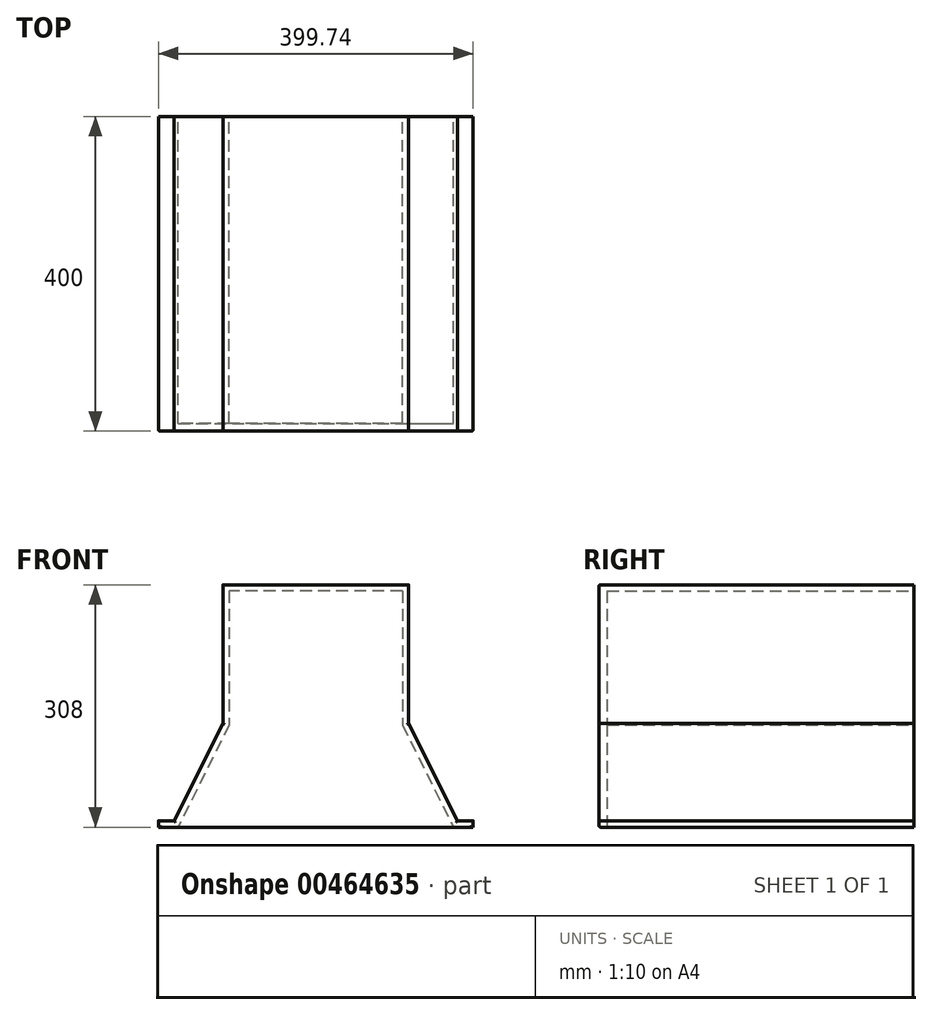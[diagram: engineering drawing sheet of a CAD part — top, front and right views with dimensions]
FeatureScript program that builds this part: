
annotation { "Feature Type Name" : "Feature", "Feature Type Description" : "" }
export const myFeature = defineFeature(function(context is Context, id is Id, definition is map)
    precondition{}
    {
        {
            var Q0;
            Q0=qCreatedBy(makeId("Front.planeOp"),FACE);
            var sketch = newSketch(context, id + "F0", { "sketchPlane" : qUnion([Q0])});
            skLineSegment(sketch, "E0", {"start": v(-131.02, -9.6) * mm, "end": v(-41.02, -9.6) * mm});
            skLineSegment(sketch, "E1.MirrorCS", {"start": v(-138.52, -1.6) * mm, "end": v(-138.52, 6.96) * mm});
            skLineSegment(sketch, "E2.MirrorCS", {"start": v(-131.02, 14.46) * mm, "end": v(-126.93, 14.46) * mm});
            skArc(sketch, "E3.MirrorCS", {"start": v(-131.02, -9.6) * mm, "mid": v(-136.51, -7.22) * mm, "end": v(-138.52, -1.6) * mm});
            skArc(sketch, "E4.MirrorCS", {"start": v(-138.52, 6.96) * mm, "mid": v(-136.33, 12.26) * mm, "end": v(-131.02, 14.46) * mm});
            skLineSegment(sketch, "E5.0", {"start": v(-131.02, 17.46) * mm, "end": v(-126.93, 17.46) * mm});
            skArc(sketch, "E5.1", {"start": v(-141.52, 6.96) * mm, "mid": v(-138.45, 14.38) * mm, "end": v(-131.02, 17.46) * mm});
            skLineSegment(sketch, "E5.2", {"start": v(-141.52, -1.5) * mm, "end": v(-141.52, 6.96) * mm});
            skArc(sketch, "E5.3", {"start": v(-141.53, -1.81) * mm, "mid": v(-141.53, -1.65) * mm, "end": v(-141.52, -1.5) * mm});
            skLineSegment(sketch, "E6", {"start": v(-93.76, -9.6) * mm, "end": v(-131.05, -9.6) * mm});
            skLineSegment(sketch, "E7.trimOffspring", {"start": v(-149.53, -9.6) * mm, "end": v(-199.87, -9.6) * mm});
            skLineSegment(sketch, "E8", {"start": v(-199.87, -9.6) * mm, "end": v(-199.87, -13.6) * mm});
            skLineSegment(sketch, "E9", {"start": v(-199.87, -13.6) * mm, "end": v(0.13, -13.6) * mm});
            skArc(sketch, "E10.filletArc", {"start": v(-149.53, -9.6) * mm, "mid": v(-143.95, -7.33) * mm, "end": v(-141.53, -1.81) * mm});
            skLineSegment(sketch, "E11", {"start": v(-49.36, -9.6) * mm, "end": v(0.13, -9.6) * mm});
            skArc(sketch, "E12.MirrorCS", {"start": v(141.8, -1.81) * mm, "mid": v(141.8, -1.65) * mm, "end": v(141.78, -1.5) * mm});
            skLineSegment(sketch, "E13.MirrorCS", {"start": v(138.78, -1.6) * mm, "end": v(138.78, 6.96) * mm});
            skLineSegment(sketch, "E14.MirrorCS", {"start": v(131.28, 14.46) * mm, "end": v(127.19, 14.46) * mm});
            skLineSegment(sketch, "E15.MirrorCS", {"start": v(200.13, -9.6) * mm, "end": v(200.13, -13.6) * mm});
            skLineSegment(sketch, "E16.MirrorCS", {"start": v(141.78, -1.5) * mm, "end": v(141.78, 6.96) * mm});
            skLineSegment(sketch, "E17.MirrorCS", {"start": v(131.28, 17.46) * mm, "end": v(127.19, 17.46) * mm});
            skArc(sketch, "E18.MirrorCS", {"start": v(131.28, -9.6) * mm, "mid": v(136.77, -7.22) * mm, "end": v(138.78, -1.6) * mm});
            skArc(sketch, "E19.MirrorCS", {"start": v(138.78, 6.96) * mm, "mid": v(136.59, 12.26) * mm, "end": v(131.28, 14.46) * mm});
            skLineSegment(sketch, "E20.MirrorCS", {"start": v(94.02, -9.6) * mm, "end": v(131.31, -9.6) * mm});
            skLineSegment(sketch, "E21.MirrorCS", {"start": v(131.28, -9.6) * mm, "end": v(41.28, -9.6) * mm});
            skLineSegment(sketch, "E22.MirrorCS", {"start": v(149.8, -9.6) * mm, "end": v(200.13, -9.6) * mm});
            skArc(sketch, "E23.MirrorCS", {"start": v(149.8, -9.6) * mm, "mid": v(144.21, -7.33) * mm, "end": v(141.8, -1.81) * mm});
            skArc(sketch, "E24.MirrorCS", {"start": v(141.78, 6.96) * mm, "mid": v(138.7, 14.38) * mm, "end": v(131.28, 17.46) * mm});
            skLineSegment(sketch, "E25", {"start": v(41.28, -9.6) * mm, "end": v(0.13, -9.6) * mm});
            skLineSegment(sketch, "E26", {"start": v(200.13, -13.6) * mm, "end": v(0.13, -13.6) * mm});
            skLineSegment(sketch, "E27", {"start": v(-126.93, 17.46) * mm, "end": v(-126.93, 14.46) * mm});
            skLineSegment(sketch, "E28", {"start": v(127.19, 17.46) * mm, "end": v(127.19, 14.46) * mm});
            skSolve(sketch);
        }
        {
            var Q0;
            Q0=qCreatedBy(makeId("Front.planeOp"),FACE);
            var sketch = newSketch(context, id + "F1", { "sketchPlane" : qUnion([Q0])});
            skLineSegment(sketch, "E29", {"start": v(-199.87, -9.6) * mm, "end": v(-174.87, -9.6) * mm});
            skLineSegment(sketch, "E30", {"start": v(-174.87, -9.6) * mm, "end": v(-110, 120.4) * mm});
            skLineSegment(sketch, "E31", {"start": v(-110, 120.4) * mm, "end": v(-110, 290.4) * mm});
            skLineSegment(sketch, "E32", {"start": v(-110, 290.4) * mm, "end": v(0, 290.4) * mm});
            skLineSegment(sketch, "E33", {"start": v(0, 0) * mm, "end": v(0, 363.05) * mm});
            skLineSegment(sketch, "E34.MirrorCS", {"start": v(110, 290.4) * mm, "end": v(0, 290.4) * mm});
            skLineSegment(sketch, "E35.MirrorCS", {"start": v(110, 120.4) * mm, "end": v(110, 290.4) * mm});
            skLineSegment(sketch, "E36.MirrorCS", {"start": v(174.87, -9.6) * mm, "end": v(110, 120.4) * mm});
            skLineSegment(sketch, "E37.MirrorCS", {"start": v(199.87, -9.6) * mm, "end": v(174.87, -9.6) * mm});
            skLineSegment(sketch, "E38.0", {"start": v(-199.87, -1.6) * mm, "end": v(-179.82, -1.6) * mm});
            skLineSegment(sketch, "E38.1", {"start": v(-179.82, -1.6) * mm, "end": v(-118, 122.29) * mm});
            skLineSegment(sketch, "E38.2", {"start": v(-118, 122.29) * mm, "end": v(-118, 298.4) * mm});
            skLineSegment(sketch, "E38.3", {"start": v(-118, 298.4) * mm, "end": v(0, 298.4) * mm});
            skLineSegment(sketch, "E38.4", {"start": v(199.87, -1.6) * mm, "end": v(179.82, -1.6) * mm});
            skLineSegment(sketch, "E38.5", {"start": v(179.82, -1.6) * mm, "end": v(118, 122.29) * mm});
            skLineSegment(sketch, "E38.6", {"start": v(118, 122.29) * mm, "end": v(118, 298.4) * mm});
            skLineSegment(sketch, "E38.7", {"start": v(118, 298.4) * mm, "end": v(0, 298.4) * mm});
            skLineSegment(sketch, "E39", {"start": v(-199.87, -9.6) * mm, "end": v(-199.87, -1.6) * mm});
            skLineSegment(sketch, "E40", {"start": v(199.87, -9.6) * mm, "end": v(199.87, -1.6) * mm});
            skSolve(sketch);
        }
        {
            var Q0;
            Q0 = qSketchRegion(id + "F1", true);
            extrude(context, id + "F2", {"entities" : qUnion([Q0]), "depth" : 400 * mm});
        }
        {
            var Q0;
            Q0=makeQuery(id+"F2.opExtrude","CAP_FACE",FACE,{"disambiguationData":[OSD([sQuery(id+"F1.wireOp",EDGE,"E29"),sQuery(id+"F1.wireOp",EDGE,"E30"),sQuery(id+"F1.wireOp",EDGE,"E31"),sQuery(id+"F1.wireOp",EDGE,"E32"),sQuery(id+"F1.wireOp",EDGE,"E34.MirrorCS"),sQuery(id+"F1.wireOp",EDGE,"E35.MirrorCS"),sQuery(id+"F1.wireOp",EDGE,"E36.MirrorCS"),sQuery(id+"F1.wireOp",EDGE,"E37.MirrorCS"),sQuery(id+"F1.wireOp",EDGE,"E38.0"),sQuery(id+"F1.wireOp",EDGE,"E38.1"),sQuery(id+"F1.wireOp",EDGE,"E38.2"),sQuery(id+"F1.wireOp",EDGE,"E38.3"),sQuery(id+"F1.wireOp",EDGE,"E38.4"),sQuery(id+"F1.wireOp",EDGE,"E38.5"),sQuery(id+"F1.wireOp",EDGE,"E38.6"),sQuery(id+"F1.wireOp",EDGE,"E38.7"),sQuery(id+"F1.wireOp",EDGE,"E39"),sQuery(id+"F1.wireOp",EDGE,"E40")])],"isStart":false});
            cPlane(context, id + "F3", {"entities" : qUnion([Q0]), "cplaneType" : CPlaneType.OFFSET, "offset" : 0 * mm, "width" : 150 * mm, "height" : 150 * mm});
        }
        {
            var Q0;
            Q0=qCreatedBy(id+"F3.planeOp",FACE);
            var sketch = newSketch(context, id + "F4", { "sketchPlane" : qUnion([Q0])});
            skLineSegment(sketch, "E41.bottom", {"start": v(-118, 298.4) * mm, "end": v(118, 298.4) * mm});
            skLineSegment(sketch, "E41.top", {"start": v(-199.87, -9.6) * mm, "end": v(199.87, -9.6) * mm});
            skLineSegment(sketch, "E42", {"start": v(-199.87, -1.6) * mm, "end": v(-179.55, -1.6) * mm});
            skLineSegment(sketch, "E43", {"start": v(118, 298.4) * mm, "end": v(118, 122.29) * mm});
            skLineSegment(sketch, "E44", {"start": v(-118, 298.4) * mm, "end": v(-118, 122.29) * mm});
            skLineSegment(sketch, "E45.trimOffspring", {"start": v(-199.87, -1.6) * mm, "end": v(-199.87, -9.6) * mm});
            skLineSegment(sketch, "E46.trimOffspring", {"start": v(199.87, -1.6) * mm, "end": v(199.87, -9.6) * mm});
            skLineSegment(sketch, "E47", {"start": v(118, 122.29) * mm, "end": v(179.77, -1.6) * mm});
            skLineSegment(sketch, "E48", {"start": v(-118, 122.29) * mm, "end": v(-179.55, -1.6) * mm});
            skLineSegment(sketch, "E49.trimOffspring", {"start": v(179.77, -1.6) * mm, "end": v(199.87, -1.6) * mm});
            skSolve(sketch);
        }
        {
            var Q0;
            Q0 = qSketchRegion(id + "F4", true);
            extrude(context, id + "F5", {"entities" : qUnion([Q0]), "oppositeDirection" : true, "depth" : 10 * mm});
        }
        {
            var Q0;
            Q0=makeQuery(id+"F2.opExtrude","SWEPT_BODY",BODY,{"disambiguationData":[OSD([sQuery(id+"F1.wireOp",EDGE,"E29"),sQuery(id+"F1.wireOp",EDGE,"E30"),sQuery(id+"F1.wireOp",EDGE,"E31"),sQuery(id+"F1.wireOp",EDGE,"E32"),sQuery(id+"F1.wireOp",EDGE,"E34.MirrorCS"),sQuery(id+"F1.wireOp",EDGE,"E35.MirrorCS"),sQuery(id+"F1.wireOp",EDGE,"E36.MirrorCS"),sQuery(id+"F1.wireOp",EDGE,"E37.MirrorCS"),sQuery(id+"F1.wireOp",EDGE,"E38.0"),sQuery(id+"F1.wireOp",EDGE,"E38.1"),sQuery(id+"F1.wireOp",EDGE,"E38.2"),sQuery(id+"F1.wireOp",EDGE,"E38.3"),sQuery(id+"F1.wireOp",EDGE,"E38.4"),sQuery(id+"F1.wireOp",EDGE,"E38.5"),sQuery(id+"F1.wireOp",EDGE,"E38.6"),sQuery(id+"F1.wireOp",EDGE,"E38.7"),sQuery(id+"F1.wireOp",EDGE,"E39"),sQuery(id+"F1.wireOp",EDGE,"E40")])]});
            var Q1;
            Q1=makeQuery(id+"F5.opExtrude","SWEPT_BODY",BODY,{"disambiguationData":[OSD([sQuery(id+"F4.wireOp",EDGE,"E41.bottom"),sQuery(id+"F4.wireOp",EDGE,"E41.top"),sQuery(id+"F4.wireOp",EDGE,"E41.left"),sQuery(id+"F4.wireOp",EDGE,"E41.right")])]});
            booleanBodies(context, id + "F6", {"operationType" : BooleanOperationType.SUBTRACTION, "tools" : qUnion([Q0]), "targets" : qUnion([Q1]), "keepTools" : true});
        }
        {
            var Q0;
            Q0=makeQuery(id+"F5.opExtrude","SWEPT_BODY",BODY,{"disambiguationData":[OSD([sQuery(id+"F4.wireOp",EDGE,"E41.bottom"),sQuery(id+"F4.wireOp",EDGE,"E41.top"),sQuery(id+"F4.wireOp",EDGE,"E42"),sQuery(id+"F4.wireOp",EDGE,"E43"),sQuery(id+"F4.wireOp",EDGE,"E44"),sQuery(id+"F4.wireOp",EDGE,"E45.trimOffspring"),sQuery(id+"F4.wireOp",EDGE,"E46.trimOffspring"),sQuery(id+"F4.wireOp",EDGE,"E47"),sQuery(id+"F4.wireOp",EDGE,"E48"),sQuery(id+"F4.wireOp",EDGE,"E49.trimOffspring")])]});
            var Q1;
            Q1=makeQuery(id+"F2.opExtrude","SWEPT_BODY",BODY,{"disambiguationData":[OSD([sQuery(id+"F1.wireOp",EDGE,"E29"),sQuery(id+"F1.wireOp",EDGE,"E30"),sQuery(id+"F1.wireOp",EDGE,"E31"),sQuery(id+"F1.wireOp",EDGE,"E32"),sQuery(id+"F1.wireOp",EDGE,"E34.MirrorCS"),sQuery(id+"F1.wireOp",EDGE,"E35.MirrorCS"),sQuery(id+"F1.wireOp",EDGE,"E36.MirrorCS"),sQuery(id+"F1.wireOp",EDGE,"E37.MirrorCS"),sQuery(id+"F1.wireOp",EDGE,"E38.0"),sQuery(id+"F1.wireOp",EDGE,"E38.1"),sQuery(id+"F1.wireOp",EDGE,"E38.2"),sQuery(id+"F1.wireOp",EDGE,"E38.3"),sQuery(id+"F1.wireOp",EDGE,"E38.4"),sQuery(id+"F1.wireOp",EDGE,"E38.5"),sQuery(id+"F1.wireOp",EDGE,"E38.6"),sQuery(id+"F1.wireOp",EDGE,"E38.7"),sQuery(id+"F1.wireOp",EDGE,"E39"),sQuery(id+"F1.wireOp",EDGE,"E40")])]});
            booleanBodies(context, id + "F7", {"operationType" : BooleanOperationType.UNION, "tools" : qUnion([Q0, Q1])});
        }
        {
            var Q0;
            Q0=makeQuery(id+"F7.opBoolean","MERGE",FACE,{"derivedFrom":[makeQuery(id+"F2.opExtrude","CAP_FACE",FACE,{"disambiguationData":[OSD([sQuery(id+"F1.wireOp",EDGE,"E29"),sQuery(id+"F1.wireOp",EDGE,"E30"),sQuery(id+"F1.wireOp",EDGE,"E31"),sQuery(id+"F1.wireOp",EDGE,"E32"),sQuery(id+"F1.wireOp",EDGE,"E34.MirrorCS"),sQuery(id+"F1.wireOp",EDGE,"E35.MirrorCS"),sQuery(id+"F1.wireOp",EDGE,"E36.MirrorCS"),sQuery(id+"F1.wireOp",EDGE,"E37.MirrorCS"),sQuery(id+"F1.wireOp",EDGE,"E38.0"),sQuery(id+"F1.wireOp",EDGE,"E38.1"),sQuery(id+"F1.wireOp",EDGE,"E38.2"),sQuery(id+"F1.wireOp",EDGE,"E38.3"),sQuery(id+"F1.wireOp",EDGE,"E38.4"),sQuery(id+"F1.wireOp",EDGE,"E38.5"),sQuery(id+"F1.wireOp",EDGE,"E38.6"),sQuery(id+"F1.wireOp",EDGE,"E38.7"),sQuery(id+"F1.wireOp",EDGE,"E39"),sQuery(id+"F1.wireOp",EDGE,"E40")])],"isStart":false}),makeQuery(id+"F5.opExtrude","CAP_FACE",FACE,{"disambiguationData":[OSD([sQuery(id+"F4.wireOp",EDGE,"E41.bottom"),sQuery(id+"F4.wireOp",EDGE,"E41.top"),sQuery(id+"F4.wireOp",EDGE,"E42"),sQuery(id+"F4.wireOp",EDGE,"E43"),sQuery(id+"F4.wireOp",EDGE,"E44"),sQuery(id+"F4.wireOp",EDGE,"E45.trimOffspring"),sQuery(id+"F4.wireOp",EDGE,"E46.trimOffspring"),sQuery(id+"F4.wireOp",EDGE,"E47"),sQuery(id+"F4.wireOp",EDGE,"E48"),sQuery(id+"F4.wireOp",EDGE,"E49.trimOffspring")])],"isStart":true})]});
            fillet(context, id + "F8", {"entities" : qUnion([Q0]), "radius" : 2 * mm, "tangentPropagation" : true, "allowEdgeOverflow" : false});
        }
    });
